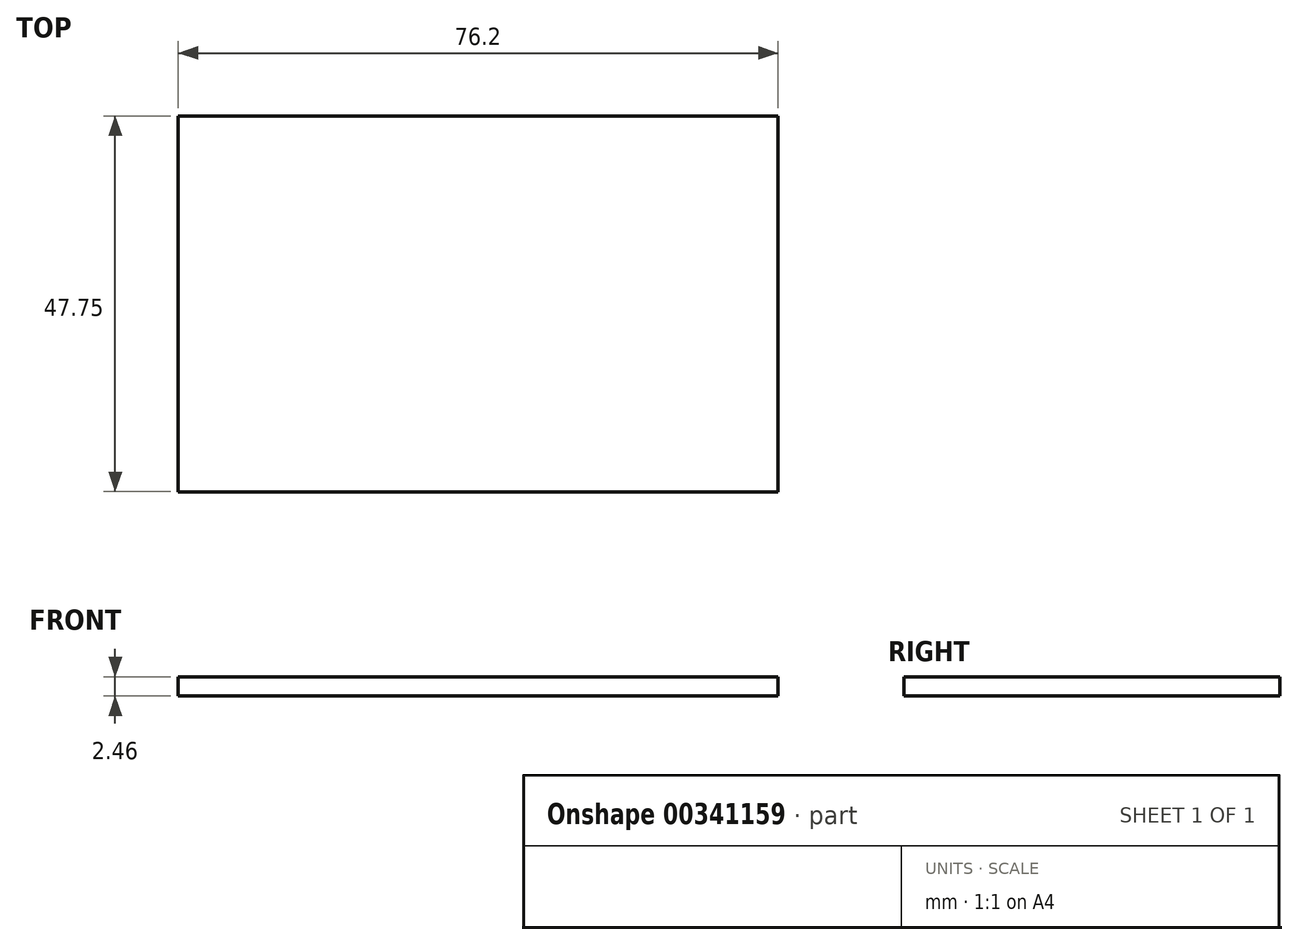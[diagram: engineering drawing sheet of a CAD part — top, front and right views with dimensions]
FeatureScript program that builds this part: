
annotation { "Feature Type Name" : "Feature", "Feature Type Description" : "" }
export const myFeature = defineFeature(function(context is Context, id is Id, definition is map)
    precondition{}
    {
        {
            var Q0;
            Q0=qCreatedBy(makeId("Top.planeOp"),FACE);
            var sketch = newSketch(context, id + "F0", { "sketchPlane" : qUnion([Q0])});
            skLineSegment(sketch, "E0.bottom", {"start": v(-49.35, 17.91) * mm, "end": v(26.85, 17.91) * mm});
            skLineSegment(sketch, "E0.top", {"start": v(-49.35, -29.84) * mm, "end": v(26.85, -29.84) * mm});
            skLineSegment(sketch, "E0.left", {"start": v(-49.35, 17.91) * mm, "end": v(-49.35, -29.84) * mm});
            skLineSegment(sketch, "E0.right", {"start": v(26.85, 17.91) * mm, "end": v(26.85, -29.84) * mm});
            skSolve(sketch);
        }
        {
            var Q0;
            Q0 = qSketchRegion(id + "F0", true);
            extrude(context, id + "F1", {"entities" : qUnion([Q0]), "depth" : 2.46 * mm});
        }
    });
